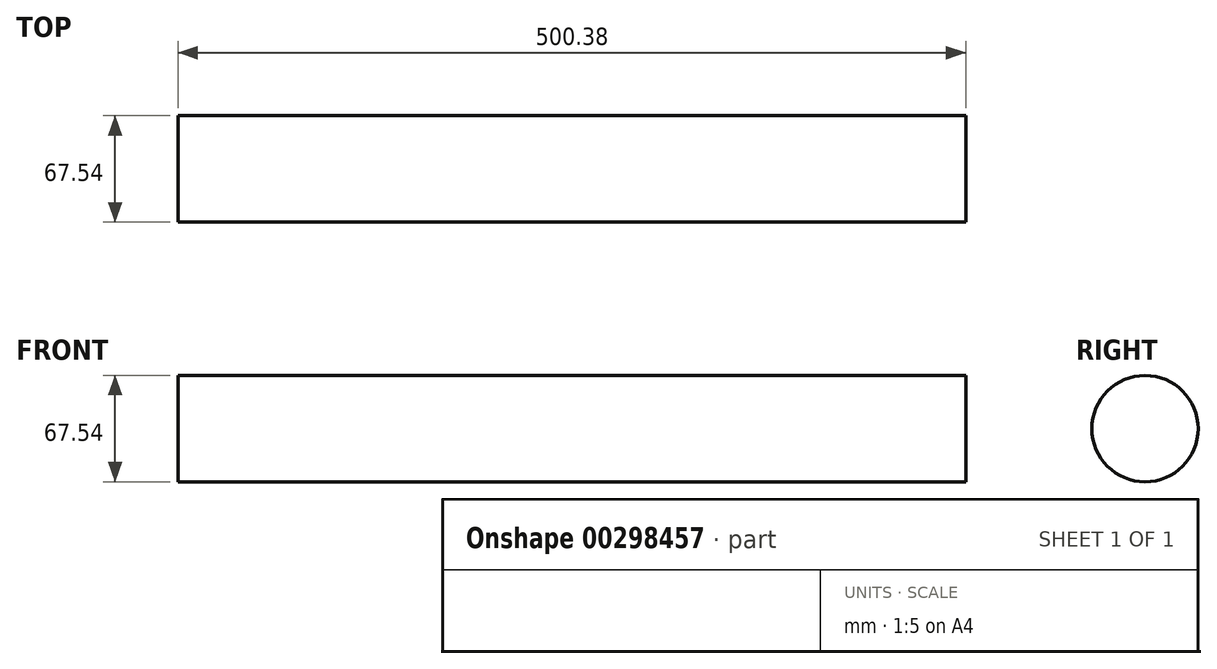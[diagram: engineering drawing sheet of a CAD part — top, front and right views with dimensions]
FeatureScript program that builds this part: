
annotation { "Feature Type Name" : "Feature", "Feature Type Description" : "" }
export const myFeature = defineFeature(function(context is Context, id is Id, definition is map)
    precondition{}
    {
        {
            var Q0;
            Q0=qCreatedBy(makeId("Right.planeOp"),FACE);
            var sketch = newSketch(context, id + "F0", { "sketchPlane" : qUnion([Q0])});
            skCircle(sketch, "E0", {"center": v(0, 0) * mm, "radius": 33.77 * mm});
            skSolve(sketch);
        }
        {
            var Q0;
            Q0 = qSketchRegion(id + "F0", true);
            extrude(context, id + "F1", {"entities" : qUnion([Q0]), "depth" : 500.38 * mm});
        }
    });
